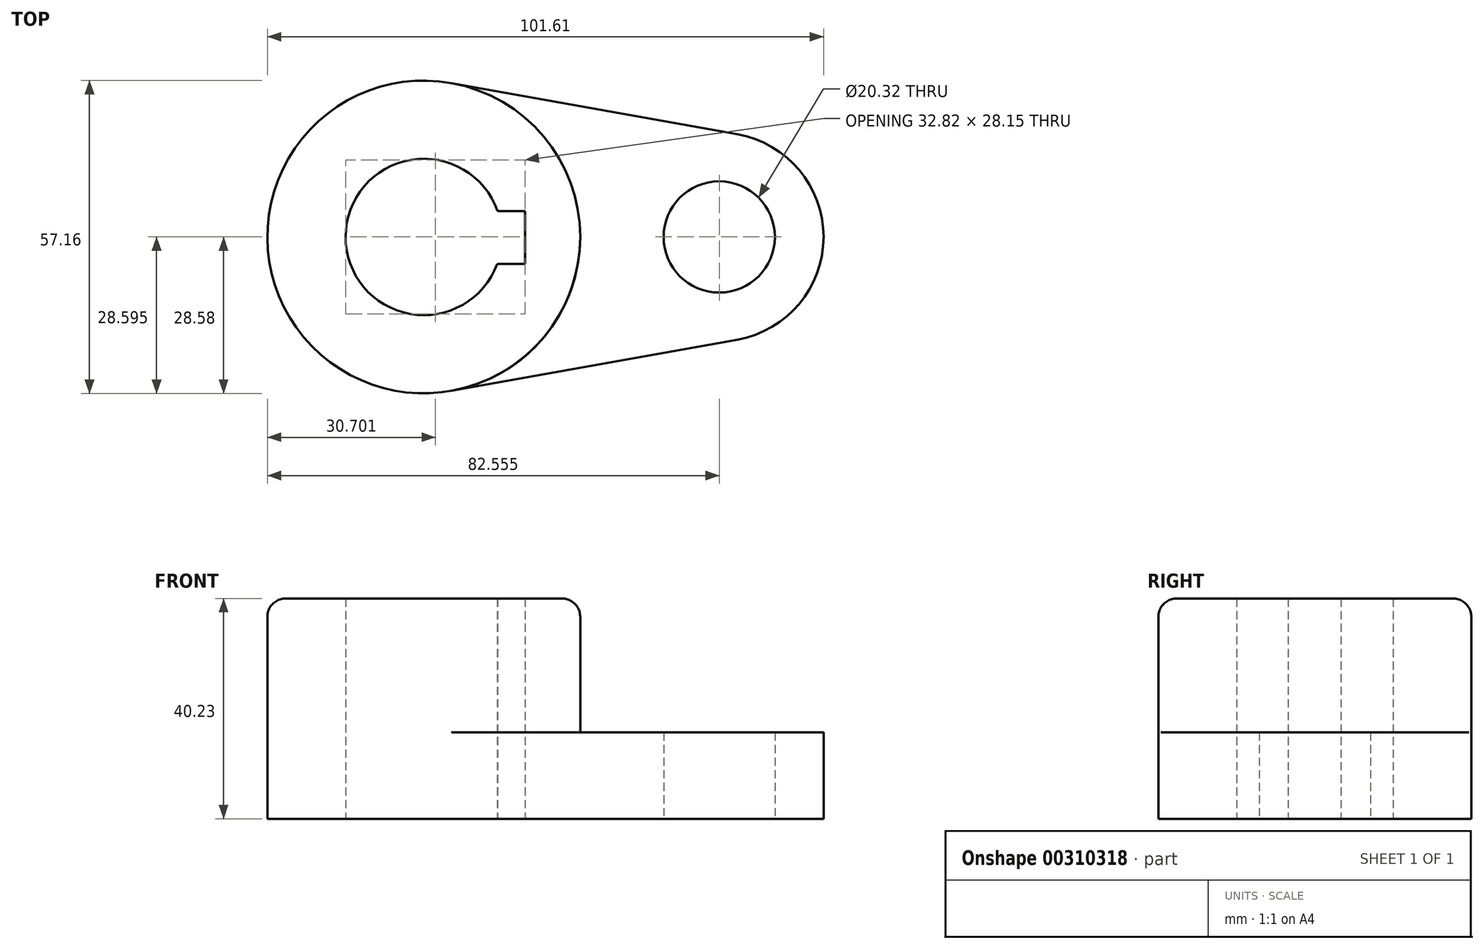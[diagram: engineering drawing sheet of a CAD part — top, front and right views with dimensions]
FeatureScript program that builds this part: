
annotation { "Feature Type Name" : "Feature", "Feature Type Description" : "" }
export const myFeature = defineFeature(function(context is Context, id is Id, definition is map)
    precondition{}
    {
        {
            var Q0;
            Q0=qCreatedBy(makeId("Top.planeOp"),FACE);
            var sketch = newSketch(context, id + "F0", { "sketchPlane" : qUnion([Q0])});
            skCircle(sketch, "E0", {"center": v(0, 0) * mm, "radius": 28.58 * mm});
            skCircle(sketch, "E1", {"center": v(53.98, 0) * mm, "radius": 19.05 * mm});
            skLineSegment(sketch, "E2", {"start": v(5.04, 28.13) * mm, "end": v(57.34, 18.75) * mm});
            skLineSegment(sketch, "E3", {"start": v(5.04, -28.13) * mm, "end": v(57.34, -18.75) * mm});
            skCircle(sketch, "E4", {"center": v(53.98, 0) * mm, "radius": 10.16 * mm});
            skArc(sketch, "E5", {"start": v(13.48, 4.74) * mm, "mid": v(-14.29, 0.09) * mm, "end": v(13.42, -4.9) * mm});
            skLineSegment(sketch, "E6", {"start": v(18.53, 4.74) * mm, "end": v(13.48, 4.74) * mm});
            skLineSegment(sketch, "E7", {"start": v(18.53, 4.74) * mm, "end": v(18.53, -4.9) * mm});
            skLineSegment(sketch, "E8", {"start": v(18.53, -4.9) * mm, "end": v(13.42, -4.9) * mm});
            skSolve(sketch);
        }
        {
            var Q0;
            Q0=makeQuery(id+"F0.imprint","IMPRINT",FACE,{"disambiguationData":[TD([[makeQuery(id+"F0.imprint","IMPRINT",EDGE,{"derivedFrom":sQuery(id+"F0.wireOp",EDGE,"E5")}),-1.0]])]});
            extrude(context, id + "F1", {"entities" : qUnion([Q0]), "depth" : 40.23 * mm});
        }
        {
            var Q0;
            Q0=makeQuery(id+"F0.imprint","IMPRINT",FACE,{"disambiguationData":[TD([[makeQuery(id+"F0.imprint","IMPRINT",EDGE,{"derivedFrom":sQuery(id+"F0.wireOp",EDGE,"E4")}),-1.0]])]});
            var Q1;
            {var subQ0=sQuery(id+"F0.wireOp",EDGE,"E2");Q1=makeQuery(id+"F0.imprint","IMPRINT",FACE,{"disambiguationData":[TD([[makeQuery(id+"F0.imprint","IMPRINT",EDGE,{"derivedFrom":subQ0}),-1.0]])]});}
            extrude(context, id + "F2", {"entities" : qUnion([Q0, Q1]), "operationType" : NewBodyOperationType.ADD, "depth" : 15.77 * mm});
        }
        {
            var Q0;
            Q0=makeQuery(id+"F1.opExtrude","CAP_EDGE",EDGE,{"disambiguationData":[OSD([sQuery(id+"F0.wireOp",EDGE,"E0")])],"isStart":false});
            fillet(context, id + "F3", {"entities" : qUnion([Q0]), "radius" : 3.3 * mm, "tangentPropagation" : true, "allowEdgeOverflow" : false});
        }
    });
